# Revit family: Toilet-American_Standard-Madera-3451.511
name_source: partatom
category: Plumbing Fixtures
units: mm (PartAtom-declared; Revit-internal decimal feet)

## family parameters
Cut with Voids When Loaded = No
Host = Face
OmniClass Number = 23.45.05.21.11.11
OmniClass Title = Water Operated Water Closets
Part Type = Normal
Room Calculation Point = No
Round Connector Dimension = Use Diameter
Shared = Yes

## types (1)
- 3451.511
    Assembly Code = D2010110
    CW Connection = Yes
    CWFU = 0
    Default Elevation = 0' - 0"
    Description = 'MADERA FloWise ELONGATED', 15" (381mm) high floor mounted, vitreous china with EverClean antimicrobial surface which inhibits the growth of stain and odor causing bacteria, mold and mildew, elongated syphon jet flush action bowl, 2-1/8" (54mm) fully glazed internal trapway, 10" x 12" (254mmx 305mm) large water surface, high efficiency 4.2 LPF (1.1 GPF) to low consumption 6 LPF (1.6 GPF), 1-1/2" (38mm) top spud and bolt caps, for use with exposed flush valve. 'SELECTRONIC' 'FloWise' Electronic 'No-Touch' Battery Flush Valve Unit, C.P. low consumption, 4.2 LPF (1.1 GPF) factory set flow, self cleaning piston operated flush valve with proximity operation and manual override, vacuum breaker, back-check angle stop, battery included, 10" (254mm) rough-in.
    HW Connection = No
    HWFU = 0
    Manufacturer = American Standard
    Model = 3451.511
    Product URL = http://www.americanstandard-us.com
    Revised Date = 12/13/2011
    URL = www.americanstandard-us.com
    Vent Connection = Yes
    WFU = 0
    Waste Connection = Yes
    Water Closet Material = Vitreous China

## geometry (parser evidence)
native form markers: Sweep x5
no freeform markers — native parametric forms only
